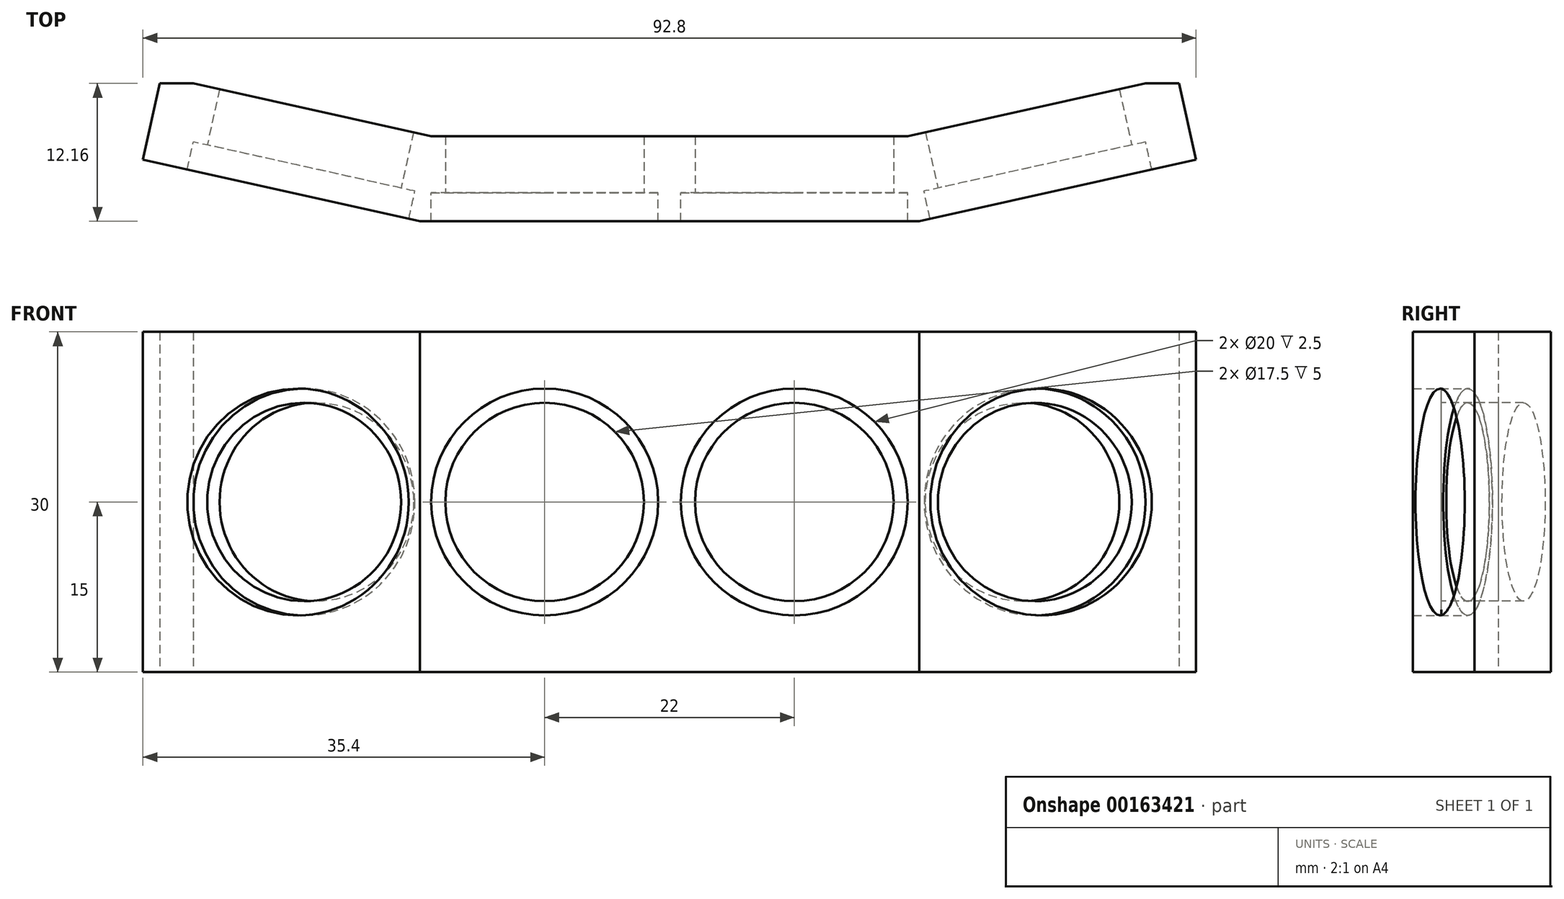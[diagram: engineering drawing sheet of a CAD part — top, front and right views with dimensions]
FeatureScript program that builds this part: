
annotation { "Feature Type Name" : "Feature", "Feature Type Description" : "" }
export const myFeature = defineFeature(function(context is Context, id is Id, definition is map)
    precondition{}
    {
        {
            var Q0;
            Q0=qCreatedBy(makeId("Top.planeOp"),FACE);
            var sketch = newSketch(context, id + "F0", { "sketchPlane" : qUnion([Q0])});
            skLineSegment(sketch, "E0", {"start": v(0, 0) * mm, "end": v(-0.98, 0.22) * mm});
            skLineSegment(sketch, "E1", {"start": v(-0.98, 0.22) * mm, "end": v(-0.43, 2.66) * mm});
            skLineSegment(sketch, "E2", {"start": v(-0.43, 2.66) * mm, "end": v(-19.96, 7) * mm});
            skLineSegment(sketch, "E3", {"start": v(-19.96, 7) * mm, "end": v(-20.5, 4.56) * mm});
            skLineSegment(sketch, "E4", {"start": v(-22.9, 12.16) * mm, "end": v(-19.96, 12.16) * mm});
            skLineSegment(sketch, "E5", {"start": v(64.5, 4.56) * mm, "end": v(63.96, 7) * mm});
            skLineSegment(sketch, "E6", {"start": v(63.96, 7) * mm, "end": v(44.43, 2.66) * mm});
            skLineSegment(sketch, "E7", {"start": v(44.43, 2.66) * mm, "end": v(44.98, 0.22) * mm});
            skLineSegment(sketch, "E8", {"start": v(44.98, 0.22) * mm, "end": v(44, 0) * mm});
            skLineSegment(sketch, "E9", {"start": v(44, 0) * mm, "end": v(43, 0) * mm});
            skLineSegment(sketch, "E10", {"start": v(43, 0) * mm, "end": v(43, 2.5) * mm});
            skLineSegment(sketch, "E11", {"start": v(43, 2.5) * mm, "end": v(23, 2.5) * mm});
            skLineSegment(sketch, "E12", {"start": v(23, 2.5) * mm, "end": v(23, 0) * mm});
            skLineSegment(sketch, "E13", {"start": v(23, 0) * mm, "end": v(21, 0) * mm});
            skLineSegment(sketch, "E14", {"start": v(21, 0) * mm, "end": v(21, 2.5) * mm});
            skLineSegment(sketch, "E15", {"start": v(21, 2.5) * mm, "end": v(1, 2.5) * mm});
            skLineSegment(sketch, "E16", {"start": v(1, 2.5) * mm, "end": v(1, 0) * mm});
            skLineSegment(sketch, "E17", {"start": v(1, 0) * mm, "end": v(0, 0) * mm});
            skLineSegment(sketch, "E18", {"start": v(-19.96, 12.16) * mm, "end": v(1, 7.5) * mm});
            skLineSegment(sketch, "E19", {"start": v(1, 7.5) * mm, "end": v(43, 7.5) * mm});
            skLineSegment(sketch, "E20", {"start": v(43, 7.5) * mm, "end": v(63.96, 12.16) * mm});
            skLineSegment(sketch, "E21", {"start": v(63.96, 12.16) * mm, "end": v(66.9, 12.16) * mm});
            skLineSegment(sketch, "E22", {"start": v(64.5, 4.56) * mm, "end": v(68.4, 5.43) * mm});
            skLineSegment(sketch, "E23", {"start": v(68.4, 5.43) * mm, "end": v(66.9, 12.16) * mm});
            skLineSegment(sketch, "E24", {"start": v(-20.5, 4.56) * mm, "end": v(-24.4, 5.43) * mm});
            skLineSegment(sketch, "E25", {"start": v(-24.4, 5.43) * mm, "end": v(-22.9, 12.16) * mm});
            skSolve(sketch);
        }
        {
            var Q0;
            Q0 = qSketchRegion(id + "F0", true);
            extrude(context, id + "F1", {"entities" : qUnion([Q0]), "depth" : 30 * mm});
        }
        {
            var Q0;
            Q0=makeQuery(id+"F1.opExtrude","SWEPT_FACE",FACE,{"disambiguationData":[OSD([sQuery(id+"F0.wireOp",EDGE,"E2")])]});
            var sketch = newSketch(context, id + "F2", { "sketchPlane" : qUnion([Q0])});
            skLineSegment(sketch, "E26.bottom", {"start": v(-21, 30) * mm, "end": v(-1, 30) * mm});
            skLineSegment(sketch, "E26.top", {"start": v(-21, 0) * mm, "end": v(-1, 0) * mm});
            skLineSegment(sketch, "E26.left", {"start": v(-21, 30) * mm, "end": v(-21, 0) * mm});
            skLineSegment(sketch, "E26.right", {"start": v(-1, 30) * mm, "end": v(-1, 0) * mm});
            skLineSegment(sketch, "E27", {"start": v(-21, 30) * mm, "end": v(-1, 0) * mm, "construction": true});
            skCircle(sketch, "E28", {"center": v(-11, 15) * mm, "radius": 10 * mm});
            skSolve(sketch);
        }
        {
            var Q0;
            {var subQ0=sQuery(id+"F2.wireOp",EDGE,"E26.top");Q0=makeQuery(id+"F2.imprint","IMPRINT",FACE,{"disambiguationData":[TD([[makeQuery(id+"F2.imprint","IMPRINT",EDGE,{"derivedFrom":subQ0}),-1.0]])]});}
            var Q1;
            {var subQ0=sQuery(id+"F2.wireOp",EDGE,"E26.bottom");Q1=makeQuery(id+"F2.imprint","IMPRINT",FACE,{"disambiguationData":[TD([[makeQuery(id+"F2.imprint","IMPRINT",EDGE,{"derivedFrom":subQ0}),1.0]])]});}
            extrude(context, id + "F3", {"entities" : qUnion([Q0, Q1]), "operationType" : NewBodyOperationType.ADD, "depth" : 2.5 * mm});
        }
        {
            var Q0;
            Q0=makeQuery(id+"F1.opExtrude","SWEPT_FACE",FACE,{"disambiguationData":[OSD([sQuery(id+"F0.wireOp",EDGE,"E15")])]});
            var sketch = newSketch(context, id + "F4", { "sketchPlane" : qUnion([Q0])});
            skLineSegment(sketch, "E29.bottom", {"start": v(1, 30) * mm, "end": v(21, 30) * mm});
            skLineSegment(sketch, "E29.top", {"start": v(1, 0) * mm, "end": v(21, 0) * mm});
            skLineSegment(sketch, "E29.left", {"start": v(1, 30) * mm, "end": v(1, 0) * mm});
            skLineSegment(sketch, "E29.right", {"start": v(21, 30) * mm, "end": v(21, 0) * mm});
            skLineSegment(sketch, "E30", {"start": v(1, 30) * mm, "end": v(21, 0) * mm, "construction": true});
            skCircle(sketch, "E31", {"center": v(11, 15) * mm, "radius": 10 * mm});
            skSolve(sketch);
        }
        {
            var Q0;
            {var subQ0=sQuery(id+"F4.wireOp",EDGE,"E29.top");Q0=makeQuery(id+"F4.imprint","IMPRINT",FACE,{"disambiguationData":[TD([[makeQuery(id+"F4.imprint","IMPRINT",EDGE,{"derivedFrom":subQ0}),-1.0]])]});}
            var Q1;
            {var subQ0=sQuery(id+"F4.wireOp",EDGE,"E29.bottom");Q1=makeQuery(id+"F4.imprint","IMPRINT",FACE,{"disambiguationData":[TD([[makeQuery(id+"F4.imprint","IMPRINT",EDGE,{"derivedFrom":subQ0}),1.0]])]});}
            extrude(context, id + "F5", {"entities" : qUnion([Q0, Q1]), "operationType" : NewBodyOperationType.ADD, "depth" : 2.5 * mm});
        }
        {
            var Q0;
            Q0=makeQuery(id+"F1.opExtrude","SWEPT_FACE",FACE,{"disambiguationData":[OSD([sQuery(id+"F0.wireOp",EDGE,"E11")])]});
            var sketch = newSketch(context, id + "F6", { "sketchPlane" : qUnion([Q0])});
            skLineSegment(sketch, "E32.bottom", {"start": v(23, 30) * mm, "end": v(43, 30) * mm});
            skLineSegment(sketch, "E32.top", {"start": v(23, 0) * mm, "end": v(43, 0) * mm});
            skLineSegment(sketch, "E32.left", {"start": v(23, 30) * mm, "end": v(23, 0) * mm});
            skLineSegment(sketch, "E32.right", {"start": v(43, 30) * mm, "end": v(43, 0) * mm});
            skLineSegment(sketch, "E33", {"start": v(23, 30) * mm, "end": v(43, 0) * mm, "construction": true});
            skCircle(sketch, "E34", {"center": v(33, 15) * mm, "radius": 10 * mm});
            skSolve(sketch);
        }
        {
            var Q0;
            {var subQ0=sQuery(id+"F6.wireOp",EDGE,"E32.bottom");Q0=makeQuery(id+"F6.imprint","IMPRINT",FACE,{"disambiguationData":[TD([[makeQuery(id+"F6.imprint","IMPRINT",EDGE,{"derivedFrom":subQ0}),1.0]])]});}
            var Q1;
            {var subQ0=sQuery(id+"F6.wireOp",EDGE,"E32.top");Q1=makeQuery(id+"F6.imprint","IMPRINT",FACE,{"disambiguationData":[TD([[makeQuery(id+"F6.imprint","IMPRINT",EDGE,{"derivedFrom":subQ0}),-1.0]])]});}
            extrude(context, id + "F7", {"entities" : qUnion([Q0, Q1]), "operationType" : NewBodyOperationType.ADD, "depth" : 2.5 * mm});
        }
        {
            var Q0;
            Q0=makeQuery(id+"F1.opExtrude","SWEPT_FACE",FACE,{"disambiguationData":[OSD([sQuery(id+"F0.wireOp",EDGE,"E6")])]});
            var sketch = newSketch(context, id + "F8", { "sketchPlane" : qUnion([Q0])});
            skLineSegment(sketch, "E35.bottom", {"start": v(43.95, 30) * mm, "end": v(63.95, 30) * mm});
            skLineSegment(sketch, "E35.top", {"start": v(43.95, 0) * mm, "end": v(63.95, 0) * mm});
            skLineSegment(sketch, "E35.left", {"start": v(43.95, 30) * mm, "end": v(43.95, 0) * mm});
            skLineSegment(sketch, "E35.right", {"start": v(63.95, 30) * mm, "end": v(63.95, 0) * mm});
            skLineSegment(sketch, "E36", {"start": v(43.95, 30) * mm, "end": v(63.95, 0) * mm, "construction": true});
            skCircle(sketch, "E37", {"center": v(53.95, 15) * mm, "radius": 10 * mm});
            skSolve(sketch);
        }
        {
            var Q0;
            {var subQ0=sQuery(id+"F8.wireOp",EDGE,"E35.bottom");Q0=makeQuery(id+"F8.imprint","IMPRINT",FACE,{"disambiguationData":[TD([[makeQuery(id+"F8.imprint","IMPRINT",EDGE,{"derivedFrom":subQ0}),1.0]])]});}
            var Q1;
            {var subQ0=sQuery(id+"F8.wireOp",EDGE,"E35.top");Q1=makeQuery(id+"F8.imprint","IMPRINT",FACE,{"disambiguationData":[TD([[makeQuery(id+"F8.imprint","IMPRINT",EDGE,{"derivedFrom":subQ0}),-1.0]])]});}
            extrude(context, id + "F9", {"entities" : qUnion([Q0, Q1]), "operationType" : NewBodyOperationType.ADD, "depth" : 2.5 * mm});
        }
        {
            var Q0;
            Q0=makeQuery(id+"F1.opExtrude","SWEPT_FACE",FACE,{"disambiguationData":[OSD([sQuery(id+"F0.wireOp",EDGE,"E15")])]});
            var sketch = newSketch(context, id + "F10", { "sketchPlane" : qUnion([Q0])});
            skCircle(sketch, "E38", {"center": v(11, 15) * mm, "radius": 8.75 * mm});
            skSolve(sketch);
        }
        {
            var Q0;
            Q0 = qSketchRegion(id + "F10", true);
            extrude(context, id + "F11", {"entities" : qUnion([Q0]), "operationType" : NewBodyOperationType.REMOVE, "oppositeDirection" : true, "depth" : 25.4 * mm});
        }
        {
            var Q0;
            Q0=makeQuery(id+"F1.opExtrude","SWEPT_FACE",FACE,{"disambiguationData":[OSD([sQuery(id+"F0.wireOp",EDGE,"E11")])]});
            var sketch = newSketch(context, id + "F12", { "sketchPlane" : qUnion([Q0])});
            skCircle(sketch, "E39", {"center": v(33, 15) * mm, "radius": 8.75 * mm});
            skSolve(sketch);
        }
        {
            var Q0;
            Q0 = qSketchRegion(id + "F12", true);
            extrude(context, id + "F13", {"entities" : qUnion([Q0]), "operationType" : NewBodyOperationType.REMOVE, "oppositeDirection" : true, "depth" : 25.4 * mm});
        }
        {
            var Q0;
            Q0=makeQuery(id+"F1.opExtrude","SWEPT_FACE",FACE,{"disambiguationData":[OSD([sQuery(id+"F0.wireOp",EDGE,"E6")])]});
            var sketch = newSketch(context, id + "F14", { "sketchPlane" : qUnion([Q0])});
            skCircle(sketch, "E40", {"center": v(53.95, 15) * mm, "radius": 8.75 * mm});
            skSolve(sketch);
        }
        {
            var Q0;
            Q0 = qSketchRegion(id + "F14", true);
            extrude(context, id + "F15", {"entities" : qUnion([Q0]), "operationType" : NewBodyOperationType.REMOVE, "oppositeDirection" : true, "depth" : 25.4 * mm});
        }
        {
            var Q0;
            Q0=makeQuery(id+"F1.opExtrude","SWEPT_FACE",FACE,{"disambiguationData":[OSD([sQuery(id+"F0.wireOp",EDGE,"E2")])]});
            var sketch = newSketch(context, id + "F16", { "sketchPlane" : qUnion([Q0])});
            skCircle(sketch, "E41", {"center": v(-11, 15) * mm, "radius": 8.75 * mm});
            skSolve(sketch);
        }
        {
            var Q0;
            Q0 = qSketchRegion(id + "F16", true);
            extrude(context, id + "F17", {"entities" : qUnion([Q0]), "operationType" : NewBodyOperationType.REMOVE, "oppositeDirection" : true, "depth" : 25.4 * mm});
        }
    });
